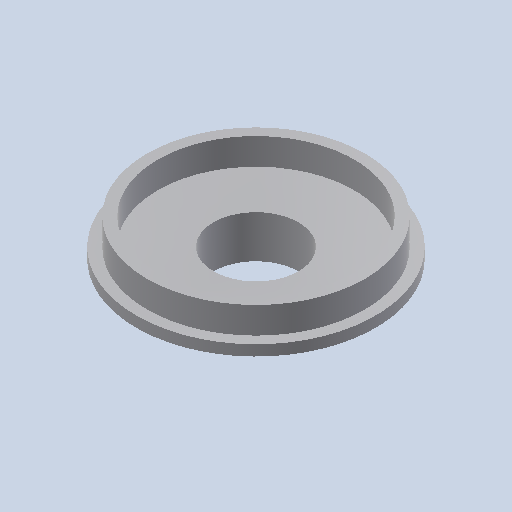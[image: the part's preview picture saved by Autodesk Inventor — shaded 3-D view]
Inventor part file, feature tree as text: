
AUTODESK INVENTOR PART (.ipt)
format: ipt  version: 2023.1 (Build 271208000, 208)  size: 117,248 bytes
history: native  units: mm
features: extrude x4, sketch x4, projected_geometry x3
ambient origin geometry x8: Origin, YZ Plane, XZ Plane, XY Plane, X Axis, Y Axis, Z Axis, Center Point
bodies: Solid1 (feature_tree)
feature tree (11):
  extrude  "Extrusion1"  Depth=2.0mm TaperAngle=0.0deg
  extrude  "Extrusion2"  Depth=2.0mm
  extrude  "Extrusion3"  Depth=5.0mm
  extrude  "Extrusion4"  Depth=2.0mm
  sketch  "Sketch1"  dims[d0=45.0mm d1=2.0mm d2=0.0mm]
  sketch  "Sketch2"  dims[d3=2.0mm d4=4.0mm]
  projected_geometry  "Projected Loop1"
  sketch  "Sketch3"  dims[d5=5.0mm d6=0.0mm d7=16.0mm]
  projected_geometry  "Projected Loop2"
  sketch  "Sketch4"  dims[d8=3.0mm d9=0.0mm d10=2.0mm d11=6.0mm d12=0.0mm]
  projected_geometry  "Projected Loop3"
